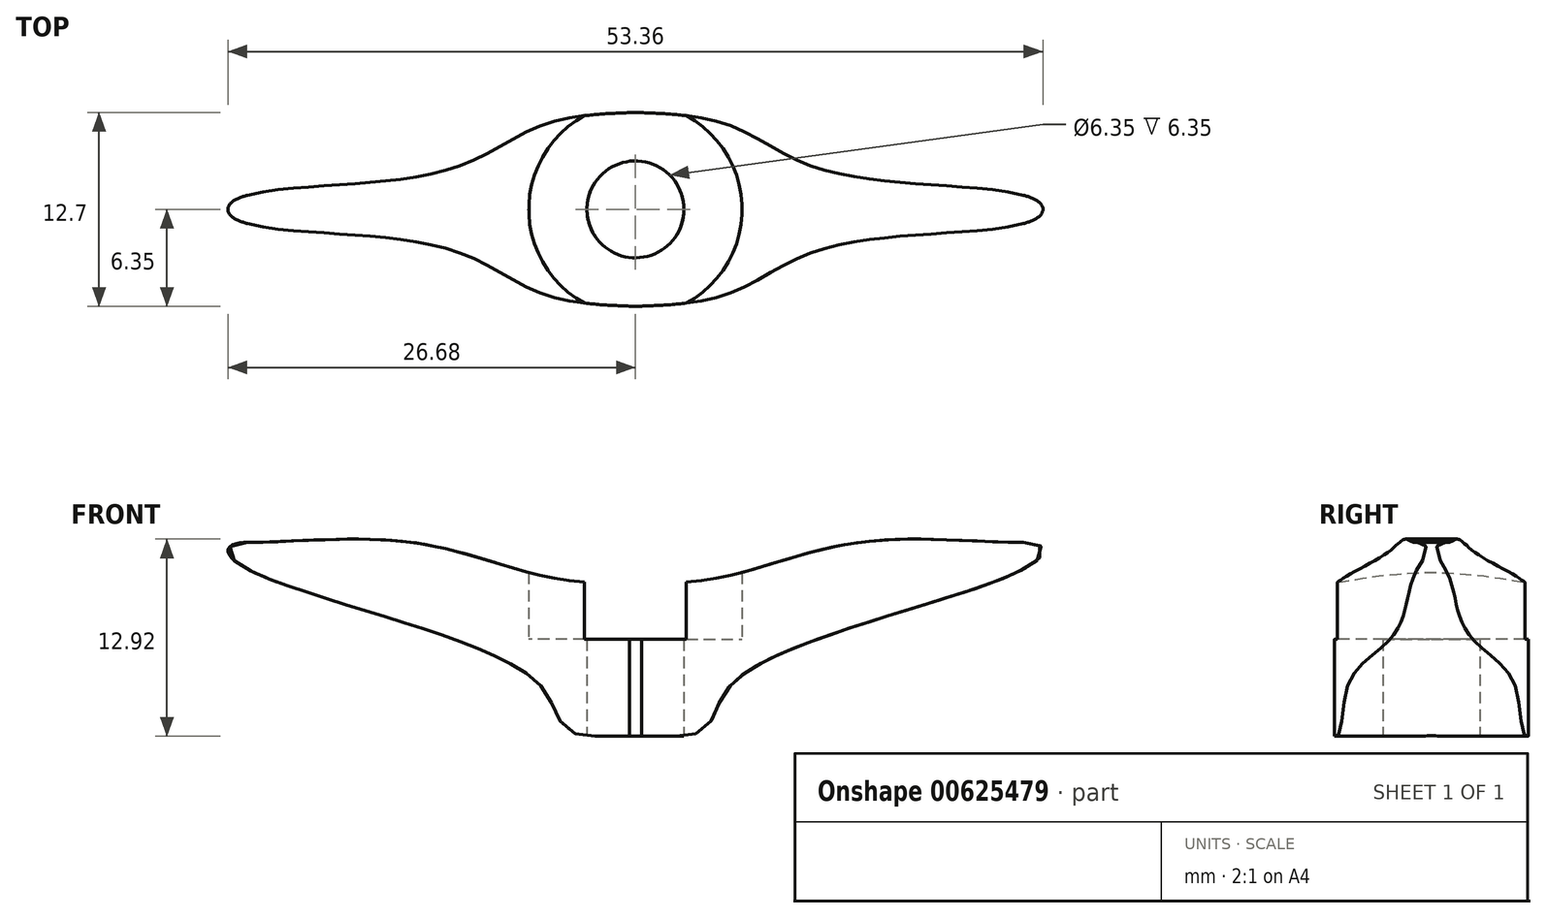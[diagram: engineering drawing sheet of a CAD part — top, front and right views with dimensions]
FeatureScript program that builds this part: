
annotation { "Feature Type Name" : "Feature", "Feature Type Description" : "" }
export const myFeature = defineFeature(function(context is Context, id is Id, definition is map)
    precondition{}
    {
        {
            var Q0;
            Q0=qCreatedBy(makeId("Front.planeOp"),FACE);
            var sketch = newSketch(context, id + "F0", { "sketchPlane" : qUnion([Q0])});
            skFitSpline(sketch, "E0", {"points": [v(-2.64, 0) * mm, v(-6.35, 3.46) * mm, v(-26.3, 11.53) * mm, v(-25.4, 12.7) * mm], "startDerivative": vector(-32.39, 0) * mm, "endDerivative": vector(28.74, 0) * mm});
            skLineSegment(sketch, "E1", {"start": v(-25.4, 12.7) * mm, "end": v(0, 12.7) * mm, "construction": true});
            skLineSegment(sketch, "E2", {"start": v(0, 12.7) * mm, "end": v(0, 0) * mm, "construction": true});
            skLineSegment(sketch, "E3", {"start": v(0, 0) * mm, "end": v(-2.64, 0) * mm});
            skLineSegment(sketch, "E4.MirrorCS", {"start": v(25.4, 12.7) * mm, "end": v(0, 12.7) * mm, "construction": true});
            skFitSpline(sketch, "E5.MirrorCS", {"points": [v(2.64, 0) * mm, v(6.35, 3.46) * mm, v(26.3, 11.53) * mm, v(25.4, 12.7) * mm], "startDerivative": vector(32.39, 0) * mm, "endDerivative": vector(-28.74, 0) * mm});
            skLineSegment(sketch, "E6.MirrorCS", {"start": v(0, 0) * mm, "end": v(2.64, 0) * mm});
            skFitSpline(sketch, "E7", {"points": [v(-25.4, 12.7) * mm, v(-14.65, 12.7) * mm, v(-5.8, 10.44) * mm, v(0, 10.01) * mm], "startDerivative": vector(25.07, 0) * mm, "endDerivative": vector(20.76, 0) * mm});
            skFitSpline(sketch, "E8.MirrorCS", {"points": [v(25.4, 12.7) * mm, v(14.65, 12.7) * mm, v(5.8, 10.44) * mm, v(0, 10.01) * mm], "startDerivative": vector(-25.07, 0) * mm, "endDerivative": vector(-20.76, 0) * mm});
            skSolve(sketch);
        }
        {
            var Q0;
            Q0=makeQuery(id+"F0.imprint","IMPRINT",FACE,{"disambiguationData":[TD([[makeQuery(id+"F0.imprint","IMPRINT",EDGE,{"derivedFrom":sQuery(id+"F0.wireOp",EDGE,"E0")}),-1.0]])]});
            extrude(context, id + "F1", {"entities" : qUnion([Q0]), "endBound" : BoundingType.SYMMETRIC, "depth" : 12.7 * mm, "offsetDistance" : 25.4 * mm});
        }
        {
            var Q0;
            Q0=qCreatedBy(makeId("Top.planeOp"),FACE);
            var sketch = newSketch(context, id + "F2", { "sketchPlane" : qUnion([Q0])});
            skCircle(sketch, "E9", {"center": v(0, 0) * mm, "radius": 6.35 * mm});
            skFitSpline(sketch, "E10", {"points": [v(0, 6.35) * mm, v(5.94, 5.58) * mm, v(10.47, 3.27) * mm, v(18.18, 1.7) * mm, v(26.69, 0) * mm], "startDerivative": vector(24.15, -0.7) * mm, "endDerivative": vector(0, -13.97) * mm});
            skPoint(sketch, "E11", {"position": v(2.64, 6.35) * mm});
            skFitSpline(sketch, "E12.MirrorCS", {"points": [v(0, -6.35) * mm, v(5.94, -5.58) * mm, v(10.47, -3.27) * mm, v(18.18, -1.7) * mm, v(26.69, 0) * mm], "startDerivative": vector(24.15, 0.7) * mm, "endDerivative": vector(0, 13.97) * mm});
            skFitSpline(sketch, "E13.MirrorCS", {"points": [v(0, 6.35) * mm, v(-5.94, 5.58) * mm, v(-10.47, 3.27) * mm, v(-18.18, 1.7) * mm, v(-26.69, 0) * mm], "startDerivative": vector(-24.15, -0.7) * mm, "endDerivative": vector(0, -13.97) * mm});
            skFitSpline(sketch, "E14.MirrorCS", {"points": [v(0, -6.35) * mm, v(-5.94, -5.58) * mm, v(-10.47, -3.27) * mm, v(-18.18, -1.7) * mm, v(-26.69, 0) * mm], "startDerivative": vector(-24.15, 0.7) * mm, "endDerivative": vector(0, 13.97) * mm});
            skLineSegment(sketch, "E15.bottom", {"start": v(28.07, 10.97) * mm, "end": v(-28.07, 10.97) * mm});
            skLineSegment(sketch, "E15.top", {"start": v(28.07, -10.97) * mm, "end": v(-28.07, -10.97) * mm});
            skLineSegment(sketch, "E16", {"start": v(28.07, 10.97) * mm, "end": v(28.07, -10.97) * mm});
            skLineSegment(sketch, "E17", {"start": v(-28.07, 10.97) * mm, "end": v(-28.07, -10.97) * mm});
            skSolve(sketch);
        }
        {
            var Q0;
            Q0=makeQuery(id+"F2.imprint","IMPRINT",FACE,{"disambiguationData":[TD([[makeQuery(id+"F2.imprint","IMPRINT",EDGE,{"derivedFrom":sQuery(id+"F2.wireOp",EDGE,"E15.bottom")}),1.0]])]});
            var Q1;
            {var subQ0=sQuery(id+"F2.wireOp",EDGE,"E13.MirrorCS");var subQ1=sQuery(id+"F2.wireOp",EDGE,"E9");var subQ5=makeQuery(id+"F2.imprint","INTERSECT",VERTEX,{"derivedFrom":[subQ1,subQ0]});Q1=makeQuery(id+"F2.imprint","IMPRINT",FACE,{"disambiguationData":[TD([[makeQuery(id+"F2.imprint","IMPRINT",EDGE,{"disambiguationData":[TD([[subQ5,-1.0]])],"derivedFrom":subQ0}),-1.0]])]});}
            var Q2;
            {var subQ0=sQuery(id+"F2.wireOp",EDGE,"E14.MirrorCS");var subQ1=sQuery(id+"F2.wireOp",EDGE,"E9");var subQ5=makeQuery(id+"F2.imprint","INTERSECT",VERTEX,{"derivedFrom":[subQ1,subQ0]});Q2=makeQuery(id+"F2.imprint","IMPRINT",FACE,{"disambiguationData":[TD([[makeQuery(id+"F2.imprint","IMPRINT",EDGE,{"disambiguationData":[TD([[subQ5,-1.0]])],"derivedFrom":subQ0}),1.0]])]});}
            var Q3;
            {var subQ0=sQuery(id+"F2.wireOp",EDGE,"E10");var subQ1=sQuery(id+"F2.wireOp",EDGE,"E9");var subQ5=makeQuery(id+"F2.imprint","INTERSECT",VERTEX,{"derivedFrom":[subQ1,subQ0]});Q3=makeQuery(id+"F2.imprint","IMPRINT",FACE,{"disambiguationData":[TD([[makeQuery(id+"F2.imprint","IMPRINT",EDGE,{"disambiguationData":[TD([[subQ5,-1.0]])],"derivedFrom":subQ0}),1.0]])]});}
            var Q4;
            {var subQ0=sQuery(id+"F2.wireOp",EDGE,"E12.MirrorCS");var subQ1=sQuery(id+"F2.wireOp",EDGE,"E9");var subQ5=makeQuery(id+"F2.imprint","INTERSECT",VERTEX,{"derivedFrom":[subQ1,subQ0]});Q4=makeQuery(id+"F2.imprint","IMPRINT",FACE,{"disambiguationData":[TD([[makeQuery(id+"F2.imprint","IMPRINT",EDGE,{"disambiguationData":[TD([[subQ5,-1.0]])],"derivedFrom":subQ0}),-1.0]])]});}
            extrude(context, id + "F3", {"entities" : qUnion([Q0, Q1, Q2, Q3, Q4]), "operationType" : NewBodyOperationType.REMOVE, "endBound" : BoundingType.THROUGH_ALL, "depth" : 25.4 * mm, "offsetDistance" : 25.4 * mm});
        }
        {
            var Q0;
            Q0=qCreatedBy(makeId("Top.planeOp"),FACE);
            var sketch = newSketch(context, id + "F4", { "sketchPlane" : qUnion([Q0])});
            skCircle(sketch, "E18", {"center": v(0, 0) * mm, "radius": 3.17 * mm});
            skSolve(sketch);
        }
        {
            var Q0;
            Q0 = qSketchRegion(id + "F4", true);
            extrude(context, id + "F5", {"entities" : qUnion([Q0]), "operationType" : NewBodyOperationType.REMOVE, "endBound" : BoundingType.THROUGH_ALL, "depth" : 25.4 * mm, "offsetDistance" : 25.4 * mm});
        }
        {
            var Q0;
            Q0=qCreatedBy(makeId("Top.planeOp"),FACE);
            var sketch = newSketch(context, id + "F6", { "sketchPlane" : qUnion([Q0])});
            skCircle(sketch, "E19", {"center": v(0, 0) * mm, "radius": 6.99 * mm});
            skSolve(sketch);
        }
        {
            var Q0;
            Q0 = qSketchRegion(id + "F6", true);
            extrude(context, id + "F7", {"entities" : qUnion([Q0]), "operationType" : NewBodyOperationType.REMOVE, "depth" : 25.4 * mm, "offsetDistance" : 25.4 * mm, "hasSecondDirection" : true, "secondDirectionOppositeDirection" : false, "secondDirectionDepth" : 6.35 * mm});
        }
    });
